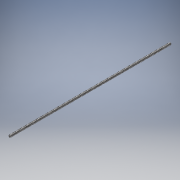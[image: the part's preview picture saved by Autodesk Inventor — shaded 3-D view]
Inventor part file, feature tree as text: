
AUTODESK INVENTOR PART (.ipt)
format: ipt  version: 2019 (Build 230136000, 136)  size: 1,142,784 bytes
history: native  units: mm
features: sketch x3, helix x2, extrude x1, chamfer x1
ambient origin geometry x8: Origin, YZ Plane, XZ Plane, XY Plane, X Axis, Y Axis, Z Axis, Center Point
bodies: Solid1 (feature_tree)
feature tree (7):
  extrude  "Extrusion1"  Depth=540.0mm TaperAngle=0.0deg
  sketch  "Sketch2"  dims[d3=1.4mm]
  chamfer  "Chamfer1"  Distance=1.0mm Angle=45.0deg
  helix  "Coil2"  [1 undecoded]
  helix  "Coil4"  [1 undecoded]
  sketch  "Sketch1"  dims[d0=8.0mm d1=540.0mm d2=0.0mm]
  sketch  "Sketch3"  dims[d4=4.0mm d13=1.0mm d14=2.0mm d15=45.0deg d16=1.4mm d17=1.4mm d18=1.4mm d19=7.0mm d20=10.0mm d21=2000.0mm d22=0.0mm d23=90.0deg d24=90.0deg d25=0.0mm d26=0.0mm d35=7.0mm d36=10.0mm d37=2000.0mm d38=0.0mm d39=90.0deg d40=90.0deg d41=0.0mm d42=0.0mm]
note: 2 required parameter values undecoded (feature->parameter linkage not recoverable at this tier; creation-order binding heuristic only, values carry confidence <= 0.55)
